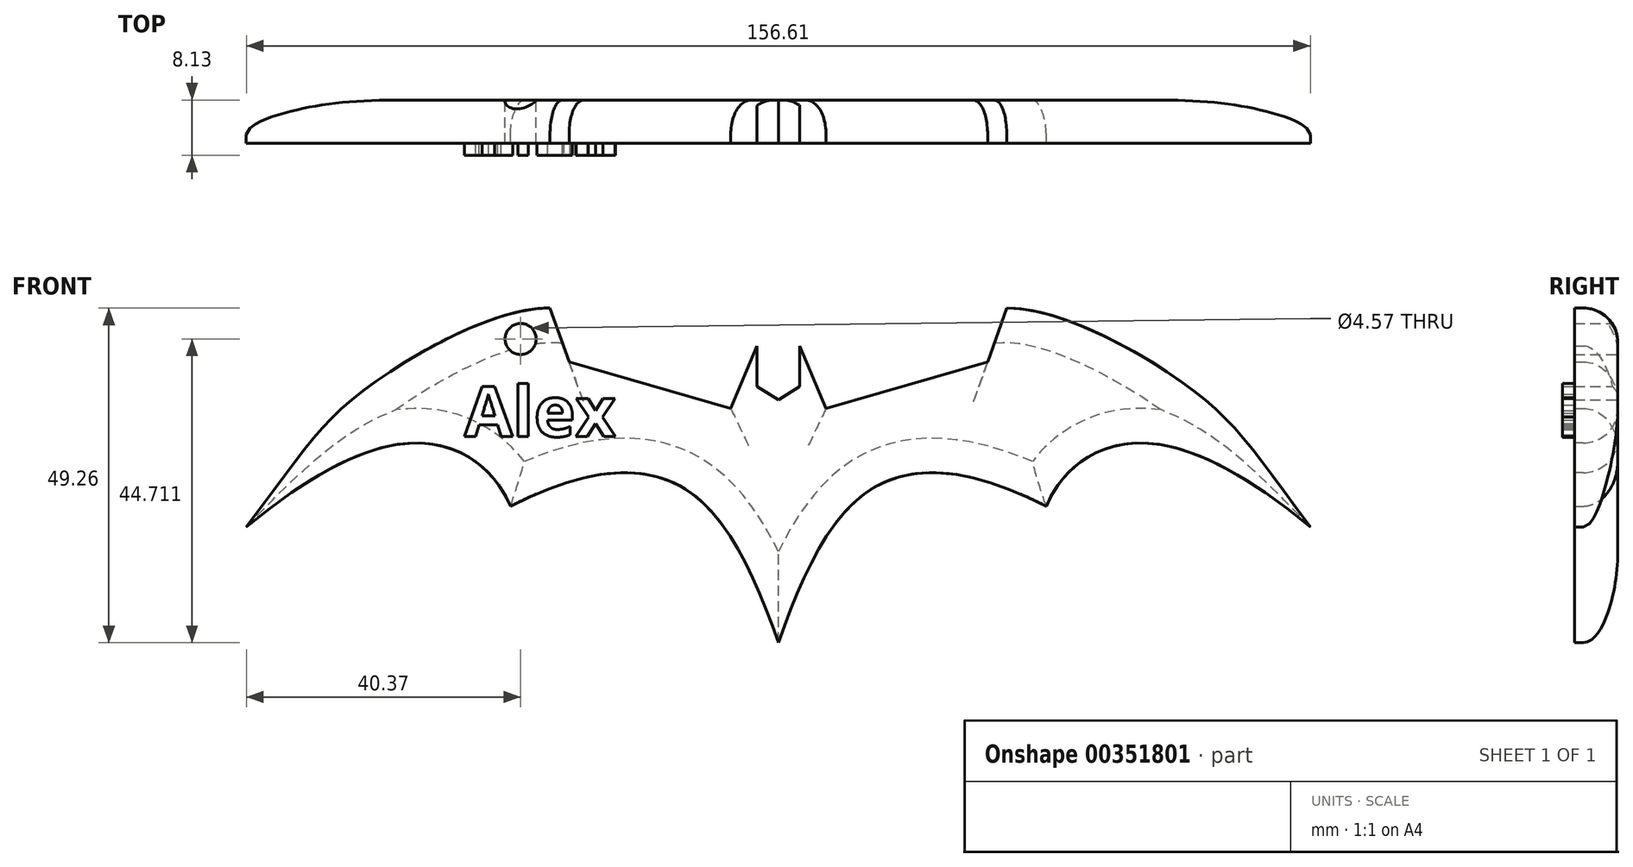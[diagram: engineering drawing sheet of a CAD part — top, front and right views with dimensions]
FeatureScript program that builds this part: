
annotation { "Feature Type Name" : "Feature", "Feature Type Description" : "" }
export const myFeature = defineFeature(function(context is Context, id is Id, definition is map)
    precondition{}
    {
        {
            var Q0;
            Q0=qCreatedBy(makeId("Front.planeOp"),FACE);
            var sketch = newSketch(context, id + "F0", { "sketchPlane" : qUnion([Q0])});
            skLineSegment(sketch, "E0", {"start": v(0.81, -22.94) * mm, "end": v(0.81, 12.8) * mm});
            skLineSegment(sketch, "E1", {"start": v(0.81, 12.8) * mm, "end": v(3.95, 14.75) * mm});
            skLineSegment(sketch, "E2", {"start": v(3.95, 14.75) * mm, "end": v(3.95, 20.77) * mm});
            skLineSegment(sketch, "E3", {"start": v(3.95, 20.77) * mm, "end": v(7.83, 11.56) * mm});
            skLineSegment(sketch, "E4", {"start": v(7.83, 11.56) * mm, "end": v(31.61, 18.42) * mm});
            skLineSegment(sketch, "E5", {"start": v(31.61, 18.42) * mm, "end": v(34.43, 26.32) * mm});
            skFitSpline(sketch, "E6", {"points": [v(34.43, 26.32) * mm, v(61.5, 14.47) * mm, v(79.12, -5.94) * mm], "startDerivative": vector(45.9, 0.7) * mm, "endDerivative": vector(51.14, -68.63) * mm});
            skFitSpline(sketch, "E7", {"points": [v(0.81, -22.94) * mm, v(14.18, -0.55) * mm, v(40.24, -2.85) * mm], "startDerivative": vector(20.43, 57.16) * mm, "endDerivative": vector(67.5, -34.6) * mm});
            skFitSpline(sketch, "E8", {"points": [v(40.24, -2.85) * mm, v(46.18, 4.24) * mm, v(79.12, -5.94) * mm], "startDerivative": vector(11.74, 26.13) * mm, "endDerivative": vector(81.37, -67.95) * mm});
            skLineSegment(sketch, "E9.MirrorCS", {"start": v(-6.21, 11.56) * mm, "end": v(-30, 18.42) * mm});
            skLineSegment(sketch, "E10.MirrorCS", {"start": v(0.81, 12.8) * mm, "end": v(-2.33, 14.75) * mm});
            skLineSegment(sketch, "E11.MirrorCS", {"start": v(-2.33, 14.75) * mm, "end": v(-2.33, 20.77) * mm});
            skLineSegment(sketch, "E12.MirrorCS", {"start": v(-2.33, 20.77) * mm, "end": v(-6.21, 11.56) * mm});
            skFitSpline(sketch, "E13.MirrorCS", {"points": [v(0.81, -22.94) * mm, v(-12.56, -0.55) * mm, v(-38.62, -2.85) * mm], "startDerivative": vector(-20.43, 57.16) * mm, "endDerivative": vector(-67.5, -34.6) * mm});
            skFitSpline(sketch, "E14.MirrorCS", {"points": [v(-38.62, -2.85) * mm, v(-44.56, 4.24) * mm, v(-77.5, -5.94) * mm], "startDerivative": vector(-11.74, 26.13) * mm, "endDerivative": vector(-81.37, -67.95) * mm});
            skFitSpline(sketch, "E15.MirrorCS", {"points": [v(-32.8, 26.32) * mm, v(-59.87, 14.47) * mm, v(-77.5, -5.94) * mm], "startDerivative": vector(-45.9, 0.7) * mm, "endDerivative": vector(-51.14, -68.63) * mm});
            skLineSegment(sketch, "E16.MirrorCS", {"start": v(-30, 18.42) * mm, "end": v(-32.8, 26.32) * mm});
            skCircle(sketch, "E17", {"center": v(-37.12, 21.77) * mm, "radius": 2.29 * mm});
            skSolve(sketch);
        }
        {
            var Q0;
            Q0=makeQuery(id+"F0.imprint","IMPRINT",FACE,{"disambiguationData":[TD([[makeQuery(id+"F0.imprint","IMPRINT",EDGE,{"derivedFrom":sQuery(id+"F0.wireOp",EDGE,"E0")}),-1.0]])]});
            var Q1;
            Q1=makeQuery(id+"F0.imprint","IMPRINT",FACE,{"disambiguationData":[TD([[makeQuery(id+"F0.imprint","IMPRINT",EDGE,{"derivedFrom":sQuery(id+"F0.wireOp",EDGE,"E0")}),1.0]])]});
            extrude(context, id + "F1", {"entities" : qUnion([Q0, Q1]), "depth" : 6.35 * mm});
        }
        {
            var Q0;
            Q0=makeQuery(id+"F1.opExtrude","CAP_FACE",FACE,{"disambiguationData":[OSD([sQuery(id+"F0.wireOp",EDGE,"E1"),sQuery(id+"F0.wireOp",EDGE,"E2"),sQuery(id+"F0.wireOp",EDGE,"E3"),sQuery(id+"F0.wireOp",EDGE,"E4"),sQuery(id+"F0.wireOp",EDGE,"E5"),sQuery(id+"F0.wireOp",EDGE,"E6"),sQuery(id+"F0.wireOp",EDGE,"E7"),sQuery(id+"F0.wireOp",EDGE,"E8"),sQuery(id+"F0.wireOp",EDGE,"E9.MirrorCS"),sQuery(id+"F0.wireOp",EDGE,"E10.MirrorCS"),sQuery(id+"F0.wireOp",EDGE,"E11.MirrorCS"),sQuery(id+"F0.wireOp",EDGE,"E12.MirrorCS"),sQuery(id+"F0.wireOp",EDGE,"E13.MirrorCS"),sQuery(id+"F0.wireOp",EDGE,"E14.MirrorCS"),sQuery(id+"F0.wireOp",EDGE,"E15.MirrorCS"),sQuery(id+"F0.wireOp",EDGE,"E16.MirrorCS"),sQuery(id+"F0.wireOp",EDGE,"d114f505-aeba-4df6-979a-efa16003b0f8")])],"isStart":false});
            var sketch = newSketch(context, id + "F2", { "sketchPlane" : qUnion([Q0])});
            skText(sketch, "E18", { "text": "Alex", "fontName": "OpenSans-Bold.ttf"});
            const initialGuessF2  = {"E18": [-0.04542, 0.0074, 1, 0, 0.00742]};
            skSetInitialGuess(sketch, initialGuessF2);
            skSolve(sketch);
        }
        {
            var Q0;
            Q0=qSketchRegion(id+"F2",true);
            extrude(context, id + "F3", {"entities" : qUnion([Q0]), "operationType" : NewBodyOperationType.ADD, "depth" : 1.78 * mm});
        }
        {
            var Q0;
            Q0=makeQuery(id+"F1.opExtrude","CAP_EDGE",EDGE,{"disambiguationData":[OSD([sQuery(id+"F0.wireOp",EDGE,"E15.MirrorCS")])],"isStart":true});
            var Q1;
            Q1=makeQuery(id+"F1.opExtrude","CAP_EDGE",EDGE,{"disambiguationData":[OSD([sQuery(id+"F0.wireOp",EDGE,"E14.MirrorCS")])],"isStart":true});
            var Q2;
            Q2=makeQuery(id+"F1.opExtrude","CAP_EDGE",EDGE,{"disambiguationData":[OSD([sQuery(id+"F0.wireOp",EDGE,"E13.MirrorCS")])],"isStart":true});
            var Q3;
            Q3=makeQuery(id+"F1.opExtrude","CAP_EDGE",EDGE,{"disambiguationData":[OSD([sQuery(id+"F0.wireOp",EDGE,"E7")])],"isStart":true});
            var Q4;
            Q4=makeQuery(id+"F1.opExtrude","CAP_EDGE",EDGE,{"disambiguationData":[OSD([sQuery(id+"F0.wireOp",EDGE,"E8")])],"isStart":true});
            var Q5;
            Q5=makeQuery(id+"F1.opExtrude","CAP_EDGE",EDGE,{"disambiguationData":[OSD([sQuery(id+"F0.wireOp",EDGE,"E6")])],"isStart":true});
            var Q6;
            Q6=makeQuery(id+"F1.opExtrude","CAP_EDGE",EDGE,{"disambiguationData":[OSD([sQuery(id+"F0.wireOp",EDGE,"E4")])],"isStart":true});
            var Q7;
            Q7=makeQuery(id+"F1.opExtrude","CAP_EDGE",EDGE,{"disambiguationData":[OSD([sQuery(id+"F0.wireOp",EDGE,"E9.MirrorCS")])],"isStart":true});
            fillet(context, id + "F4", {"entities" : qUnion([Q0, Q1, Q2, Q3, Q4, Q5, Q6, Q7]), "radius" : 5.08 * mm, "tangentPropagation" : true, "allowEdgeOverflow" : false});
        }
        {
            var Q0;
            Q0=makeQuery(id+"F1.opExtrude","CAP_EDGE",EDGE,{"disambiguationData":[OSD([sQuery(id+"F0.wireOp",EDGE,"E12.MirrorCS")])],"isStart":true});
            var Q1;
            Q1=makeQuery(id+"F1.opExtrude","CAP_EDGE",EDGE,{"disambiguationData":[OSD([sQuery(id+"F0.wireOp",EDGE,"E3")])],"isStart":true});
            fillet(context, id + "F5", {"entities" : qUnion([Q0, Q1]), "radius" : 5.08 * mm, "tangentPropagation" : true, "allowEdgeOverflow" : false});
        }
    });
